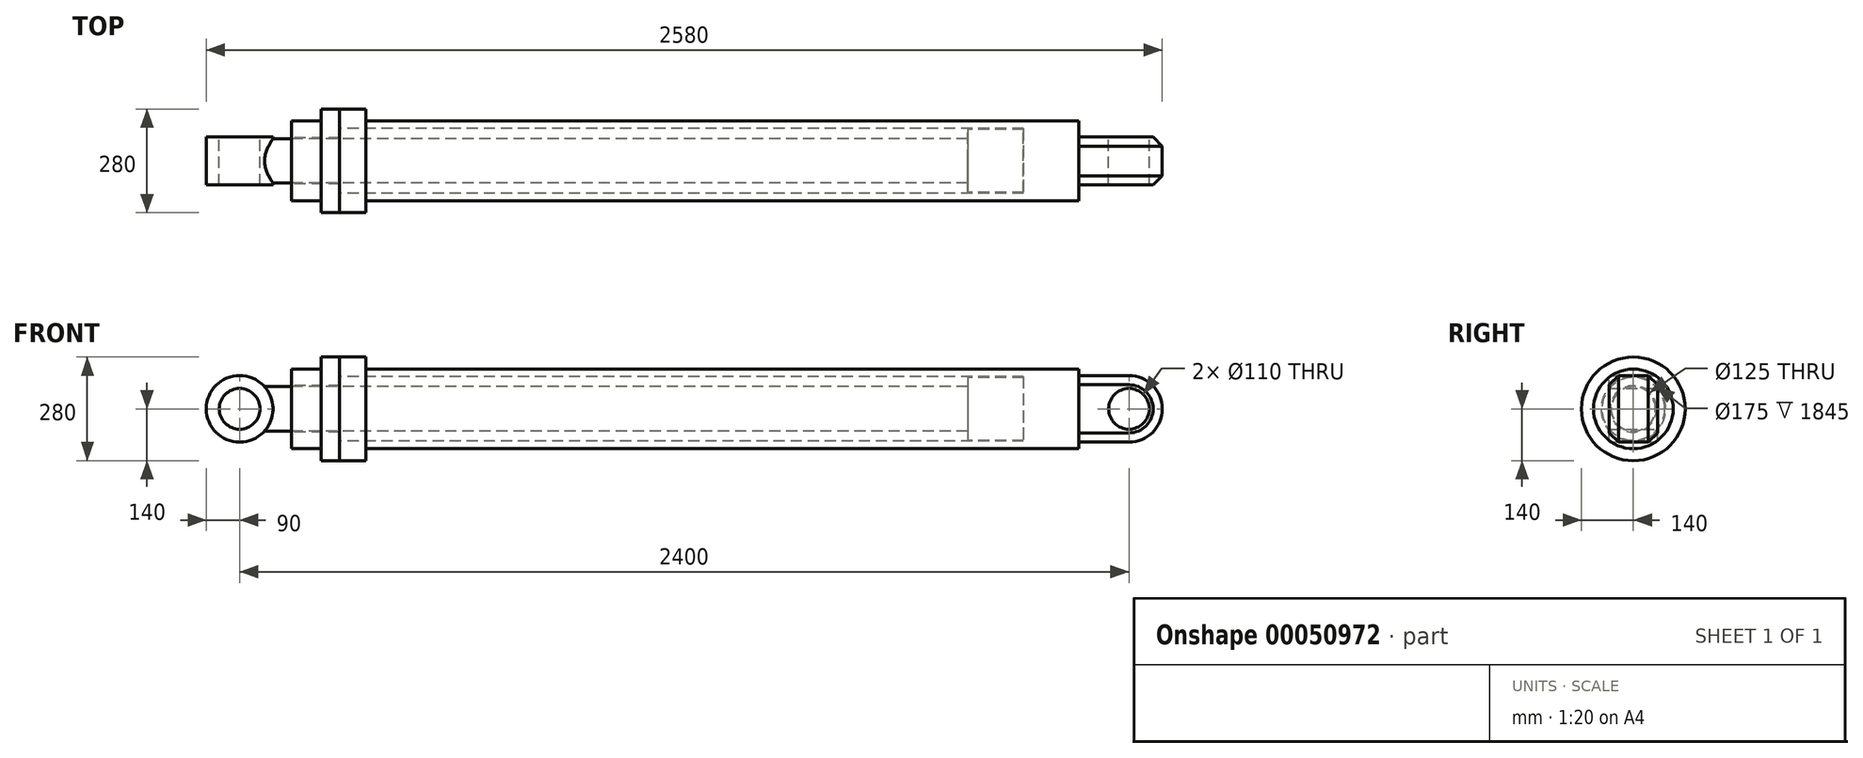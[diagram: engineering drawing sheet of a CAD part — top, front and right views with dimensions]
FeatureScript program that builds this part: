
annotation { "Feature Type Name" : "Feature", "Feature Type Description" : "" }
export const myFeature = defineFeature(function(context is Context, id is Id, definition is map)
    precondition{}
    {
        {
            var Q0;
            Q0=qCreatedBy(makeId("Front.planeOp"),FACE);
            var sketch = newSketch(context, id + "F0", { "sketchPlane" : qUnion([Q0])});
            skLineSegment(sketch, "E0", {"start": v(-3125.61, 0) * mm, "end": v(386.3, 0) * mm, "construction": true});
            skCircle(sketch, "E1", {"center": v(0, 0) * mm, "radius": 55 * mm});
            skCircle(sketch, "E2", {"center": v(0, 0) * mm, "radius": 90 * mm});
            skLineSegment(sketch, "E3", {"start": v(0, 90) * mm, "end": v(-135, 90) * mm});
            skLineSegment(sketch, "E4", {"start": v(-135, 90) * mm, "end": v(-135, 0) * mm});
            skLineSegment(sketch, "E5", {"start": v(-135, 90) * mm, "end": v(-135, 107.5) * mm});
            skLineSegment(sketch, "E6", {"start": v(-135, 107.5) * mm, "end": v(-2060, 107.5) * mm});
            skLineSegment(sketch, "E7", {"start": v(-2060, 107.5) * mm, "end": v(-2060, 87.5) * mm});
            skLineSegment(sketch, "E8", {"start": v(-2060, 107.5) * mm, "end": v(-2060, 140) * mm});
            skLineSegment(sketch, "E9", {"start": v(-2060, 140) * mm, "end": v(-2180, 140) * mm});
            skLineSegment(sketch, "E10", {"start": v(-2180, 140) * mm, "end": v(-2180, 107.5) * mm});
            skLineSegment(sketch, "E11", {"start": v(-2180, 107.5) * mm, "end": v(-2260, 107.5) * mm});
            skLineSegment(sketch, "E12", {"start": v(-2260, 107.5) * mm, "end": v(-2260, 62.5) * mm});
            skLineSegment(sketch, "E13", {"start": v(-435, 60) * mm, "end": v(-2332.92, 60) * mm});
            skCircle(sketch, "E14", {"center": v(-2400, 0) * mm, "radius": 90 * mm});
            skCircle(sketch, "E15", {"center": v(-2400, 0) * mm, "radius": 55 * mm});
            skLineSegment(sketch, "E16", {"start": v(-435, 60) * mm, "end": v(-435, 85) * mm});
            skLineSegment(sketch, "E17", {"start": v(-435, 85) * mm, "end": v(-285, 85) * mm});
            skLineSegment(sketch, "E18", {"start": v(-285, 85) * mm, "end": v(-285, 0) * mm});
            skLineSegment(sketch, "E19", {"start": v(-2300, 60) * mm, "end": v(-2300, 0) * mm});
            skLineSegment(sketch, "E20", {"start": v(-285, 85) * mm, "end": v(-285, 87.5) * mm});
            skLineSegment(sketch, "E21", {"start": v(-285, 87.5) * mm, "end": v(-2130, 87.5) * mm});
            skLineSegment(sketch, "E22", {"start": v(-2130, 140) * mm, "end": v(-2130, 62.5) * mm});
            skLineSegment(sketch, "E23", {"start": v(-2130, 62.5) * mm, "end": v(-2260, 62.5) * mm});
            skPoint(sketch, "E24.orphan", {"position": v(-2060, 0) * mm});
            skPoint(sketch, "E25.orphan", {"position": v(-2180, 0) * mm});
            skPoint(sketch, "E26.orphan", {"position": v(-2260, 0) * mm});
            skLineSegment(sketch, "E27", {"start": v(-90, 0) * mm, "end": v(-2310, 0) * mm});
            skLineSegment(sketch, "E28.MirrorCS", {"start": v(-135, -90) * mm, "end": v(-135, 0) * mm});
            skLineSegment(sketch, "E29.MirrorCS", {"start": v(0, -90) * mm, "end": v(-135, -90) * mm});
            skSolve(sketch);
        }
        {
            var Q0;
            Q0=makeQuery(id+"F0.imprint","IMPRINT",FACE,{"disambiguationData":[TD([[makeQuery(id+"F0.imprint","IMPRINT",EDGE,{"derivedFrom":sQuery(id+"F0.wireOp",EDGE,"E1")}),-1.0]])]});
            var Q1;
            {var subQ0=sQuery(id+"F0.wireOp",EDGE,"E3");Q1=makeQuery(id+"F0.imprint","IMPRINT",FACE,{"disambiguationData":[TD([[makeQuery(id+"F0.imprint","IMPRINT",EDGE,{"derivedFrom":subQ0}),1.0]])]});}
            var Q2;
            Q2=makeQuery(id+"F0.imprint","IMPRINT",FACE,{"disambiguationData":[TD([[makeQuery(id+"F0.imprint","IMPRINT",EDGE,{"derivedFrom":sQuery(id+"F0.wireOp",EDGE,"E15")}),-1.0]])]});
            var Q3;
            {var subQ4=sQuery(id+"F0.wireOp",EDGE,"E28.MirrorCS");Q3=makeQuery(id+"F0.imprint","IMPRINT",FACE,{"disambiguationData":[TD([[makeQuery(id+"F0.imprint","IMPRINT",EDGE,{"derivedFrom":subQ4}),-1.0]])]});}
            extrude(context, id + "F1", {"entities" : qUnion([Q0, Q1, Q2, Q3]), "endBound" : BoundingType.SYMMETRIC, "depth" : 130 * mm});
        }
        {
            var Q0;
            {var subQ3=sQuery(id+"F0.wireOp",EDGE,"E19");Q0=makeQuery(id+"F0.imprint","IMPRINT",FACE,{"disambiguationData":[TD([[makeQuery(id+"F0.imprint","IMPRINT",EDGE,{"derivedFrom":subQ3}),-1.0]])]});}
            var Q1;
            {var subQ3=sQuery(id+"F0.wireOp",EDGE,"E16");Q1=makeQuery(id+"F0.imprint","IMPRINT",FACE,{"disambiguationData":[TD([[makeQuery(id+"F0.imprint","IMPRINT",EDGE,{"derivedFrom":subQ3}),-1.0]])]});}
            var Q2;
            Q2=sQuery(id+"F0.wireOp",EDGE,"E0");
            revolve(context, id + "F2", {"operationType" : NewBodyOperationType.ADD, "entities" : qUnion([Q0, Q1]), "axis" : qUnion([Q2]), "revolveType" : RevolveType.FULL});
        }
        {
            var Q0;
            {var subQ4=sQuery(id+"F0.wireOp",EDGE,"E4");Q0=makeQuery(id+"F0.imprint","IMPRINT",FACE,{"disambiguationData":[TD([[makeQuery(id+"F0.imprint","IMPRINT",EDGE,{"derivedFrom":subQ4}),-1.0]])]});}
            var Q1;
            {var subQ1=sQuery(id+"F0.wireOp",EDGE,"E7");Q1=makeQuery(id+"F0.imprint","IMPRINT",FACE,{"disambiguationData":[TD([[makeQuery(id+"F0.imprint","IMPRINT",EDGE,{"derivedFrom":subQ1}),-1.0]])]});}
            var Q2;
            Q2=sQuery(id+"F0.wireOp",EDGE,"E0");
            revolve(context, id + "F3", {"operationType" : NewBodyOperationType.ADD, "entities" : qUnion([Q0, Q1]), "axis" : qUnion([Q2]), "revolveType" : RevolveType.FULL});
        }
        {
            var Q0;
            {var subQ0=sQuery(id+"F0.wireOp",EDGE,"E10");Q0=makeQuery(id+"F0.imprint","IMPRINT",FACE,{"disambiguationData":[TD([[makeQuery(id+"F0.imprint","IMPRINT",EDGE,{"derivedFrom":subQ0}),1.0]])]});}
            var Q1;
            Q1=sQuery(id+"F0.wireOp",EDGE,"E0");
            revolve(context, id + "F4", {"entities" : qUnion([Q0]), "axis" : qUnion([Q1]), "revolveType" : RevolveType.FULL});
        }
        {
            var Q0;
            Q0=makeQuery(id+"F1.opExtrude","CAP_EDGE",EDGE,{"disambiguationData":[OSD([sQuery(id+"F0.wireOp",EDGE,"E3")])],"isStart":false});
            var Q1;
            Q1=makeQuery(id+"F1.opExtrude","CAP_EDGE",EDGE,{"disambiguationData":[OSD([sQuery(id+"F0.wireOp",EDGE,"E3")])],"isStart":true});
            chamfer(context, id + "F5", {"entities" : qUnion([Q0, Q1]), "width" : 25 * mm, "tangentPropagation" : true});
        }
    });
